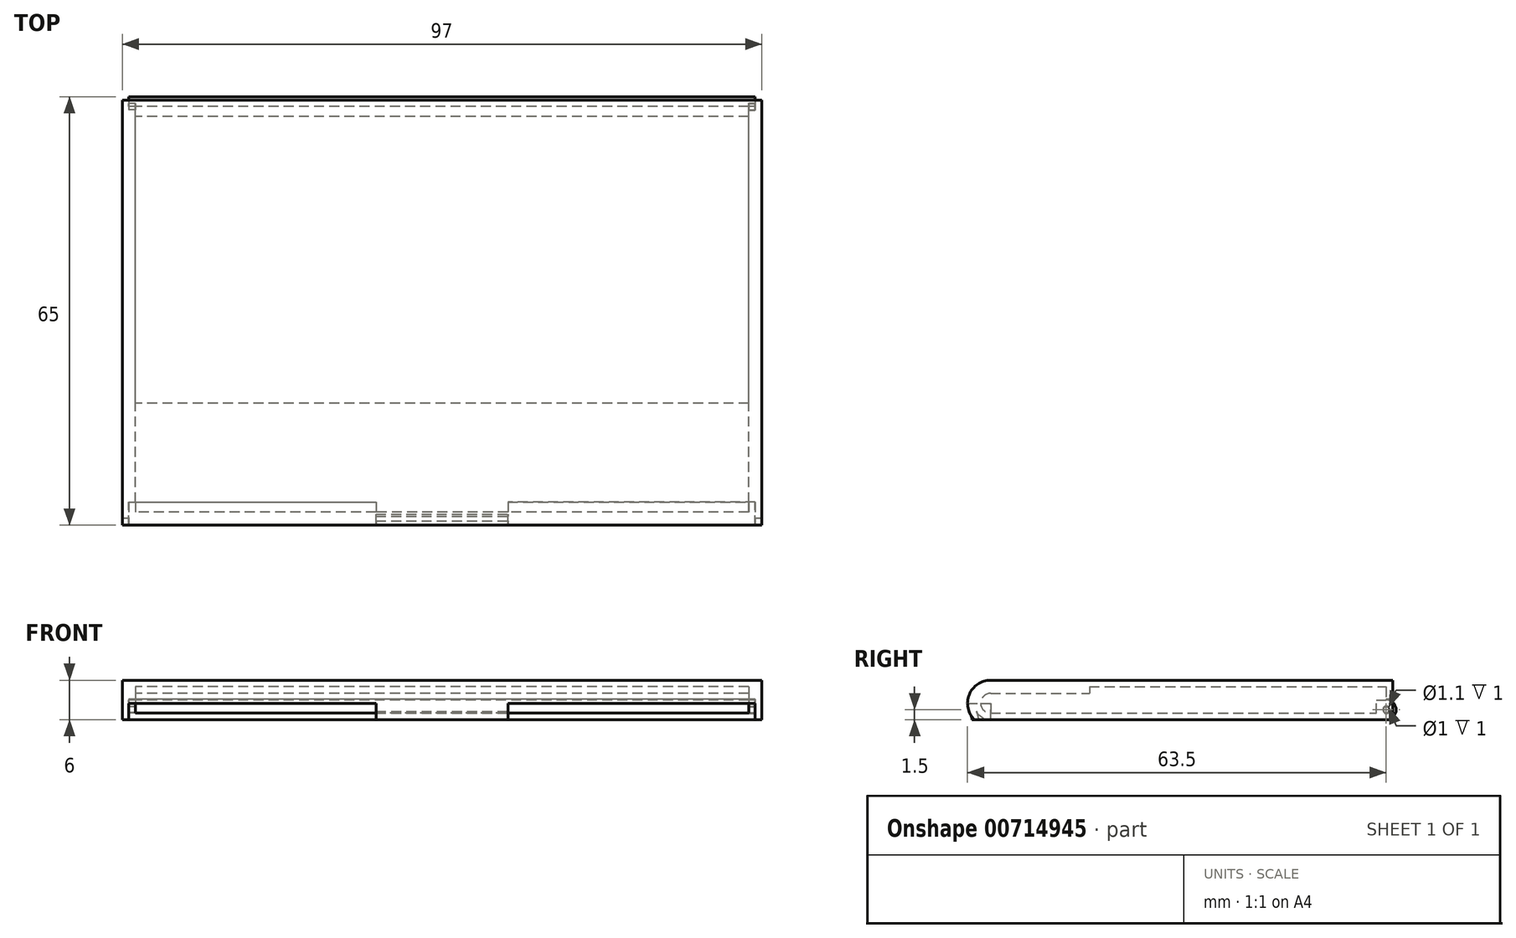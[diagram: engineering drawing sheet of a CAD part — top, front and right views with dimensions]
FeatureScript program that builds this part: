
annotation { "Feature Type Name" : "Feature", "Feature Type Description" : "" }
export const myFeature = defineFeature(function(context is Context, id is Id, definition is map)
    precondition{}
    {
        {
            var Q0;
            Q0=qCreatedBy(makeId("Right.planeOp"),FACE);
            var sketch = newSketch(context, id + "F0", { "sketchPlane" : qUnion([Q0])});
            skLineSegment(sketch, "E0", {"start": v(0, 7.84) * mm, "end": v(0, -7.77) * mm, "construction": true});
            skLineSegment(sketch, "E1", {"start": v(-35.57, 0) * mm, "end": v(44.83, 0) * mm, "construction": true});
            skLineSegment(sketch, "E2.bottom", {"start": v(-30, 2.5) * mm, "end": v(30, 2.5) * mm});
            skLineSegment(sketch, "E2.top", {"start": v(-30, -2.5) * mm, "end": v(30, -2.5) * mm});
            skArc(sketch, "E3", {"start": v(-30, 2.5) * mm, "mid": v(-32.5, 0) * mm, "end": v(-30, -2.5) * mm});
            skPoint(sketch, "E4", {"position": v(0, 2.5) * mm});
            skPoint(sketch, "E5", {"position": v(0, -2.5) * mm});
            skLineSegment(sketch, "E6", {"start": v(30, 2.5) * mm, "end": v(30, -2.5) * mm});
            skSolve(sketch);
        }
        {
            var Q0;
            Q0 = qSketchRegion(id + "F0", true);
            extrude(context, id + "F1", {"entities" : qUnion([Q0]), "endBound" : BoundingType.SYMMETRIC, "depth" : 95 * mm, "offsetDistance" : 25 * mm});
        }
        {
            var Q0;
            Q0=makeQuery(id+"F1.opExtrude","SWEPT_FACE",FACE,{"disambiguationData":[OSD([sQuery(id+"F0.wireOp",EDGE,"E2.bottom")])]});
            var Q1;
            Q1=makeQuery(id+"F1.opExtrude","SWEPT_FACE",FACE,{"disambiguationData":[OSD([sQuery(id+"F0.wireOp",EDGE,"E6")])]});
            shell(context, id + "F2", {"entities" : qUnion([Q0, Q1]), "thickness" : 1 * mm});
        }
        {
            var Q0;
            Q0=qCreatedBy(makeId("Right.planeOp"),FACE);
            var sketch = newSketch(context, id + "F3", { "sketchPlane" : qUnion([Q0])});
            skLineSegment(sketch, "E7.bottom", {"start": v(-30, 2.5) * mm, "end": v(-15, 2.5) * mm});
            skLineSegment(sketch, "E7.top", {"start": v(-30, 1.5) * mm, "end": v(-15, 1.5) * mm});
            skLineSegment(sketch, "E7.left", {"start": v(-30, 2.5) * mm, "end": v(-30, 1.5) * mm});
            skLineSegment(sketch, "E7.right", {"start": v(-15, 2.5) * mm, "end": v(-15, 1.5) * mm});
            skSolve(sketch);
        }
        {
            var Q0;
            Q0 = qSketchRegion(id + "F3", true);
            extrude(context, id + "F4", {"entities" : qUnion([Q0]), "operationType" : NewBodyOperationType.ADD, "endBound" : BoundingType.UP_TO_NEXT, "depth" : 25 * mm, "offsetDistance" : 25 * mm, "hasSecondDirection" : true, "secondDirectionBound" : SecondDirectionBoundingType.UP_TO_NEXT, "secondDirectionOppositeDirection" : true, "secondDirectionDepth" : 25 * mm});
        }
        {
            var Q0;
            Q0=qCreatedBy(makeId("Right.planeOp"),FACE);
            var sketch = newSketch(context, id + "F5", { "sketchPlane" : qUnion([Q0])});
            skArc(sketch, "E8", {"start": v(29.98, -2.5) * mm, "mid": v(31.5, -1) * mm, "end": v(30, 0.5) * mm});
            skLineSegment(sketch, "E9.bottom", {"start": v(30, 0.5) * mm, "end": v(28.5, 0.5) * mm});
            skLineSegment(sketch, "E9.top", {"start": v(30, -2.5) * mm, "end": v(28.5, -2.5) * mm});
            skLineSegment(sketch, "E9.left", {"start": v(30, 0.5) * mm, "end": v(30, -2.5) * mm});
            skLineSegment(sketch, "E9.right", {"start": v(28.5, 0.5) * mm, "end": v(28.5, -2.5) * mm});
            skSolve(sketch);
        }
        {
            var Q0;
            Q0 = qSketchRegion(id + "F5", true);
            var Q1;
            Q1=makeQuery(id+"F1.opExtrude","CAP_FACE",FACE,{"disambiguationData":[OSD([sQuery(id+"F0.wireOp",EDGE,"E2.bottom"),sQuery(id+"F0.wireOp",EDGE,"E2.top"),sQuery(id+"F0.wireOp",EDGE,"E3"),sQuery(id+"F0.wireOp",EDGE,"E6")])],"isStart":false});
            var Q2;
            Q2=makeQuery(id+"F1.opExtrude","CAP_FACE",FACE,{"disambiguationData":[OSD([sQuery(id+"F0.wireOp",EDGE,"E2.bottom"),sQuery(id+"F0.wireOp",EDGE,"E2.top"),sQuery(id+"F0.wireOp",EDGE,"E3"),sQuery(id+"F0.wireOp",EDGE,"E6")])],"isStart":true});
            extrude(context, id + "F6", {"entities" : qUnion([Q0]), "operationType" : NewBodyOperationType.ADD, "endBound" : BoundingType.UP_TO_SURFACE, "depth" : 25 * mm, "endBoundEntityFace" : qUnion([Q1]), "offsetDistance" : 25 * mm, "hasSecondDirection" : true, "secondDirectionBound" : SecondDirectionBoundingType.UP_TO_SURFACE, "secondDirectionOppositeDirection" : true, "secondDirectionDepth" : 25 * mm, "secondDirectionBoundEntityFace" : qUnion([Q2])});
        }
        {
            var Q0;
            Q0=makeQuery(id+"F6.boolean.opBoolean","MERGE",FACE,{"derivedFrom":[makeQuery(id+"F1.opExtrude","CAP_FACE",FACE,{"disambiguationData":[OSD([sQuery(id+"F0.wireOp",EDGE,"E2.bottom"),sQuery(id+"F0.wireOp",EDGE,"E2.top"),sQuery(id+"F0.wireOp",EDGE,"E3"),sQuery(id+"F0.wireOp",EDGE,"E6")])],"isStart":false}),makeQuery(id+"F6.opExtrude","CAP_FACE",FACE,{"disambiguationData":[OSD([sQuery(id+"F5.wireOp",EDGE,"E8"),sQuery(id+"F5.wireOp",EDGE,"E9.bottom"),sQuery(id+"F5.wireOp",EDGE,"E9.top"),sQuery(id+"F5.wireOp",EDGE,"E9.right")])],"isStart":false})]});
            var sketch = newSketch(context, id + "F7", { "sketchPlane" : qUnion([Q0])});
            skCircle(sketch, "E10", {"center": v(30, -1) * mm, "radius": 0.55 * mm});
            skSolve(sketch);
        }
        {
            var Q0;
            Q0 = qSketchRegion(id + "F7", true);
            extrude(context, id + "F8", {"entities" : qUnion([Q0]), "operationType" : NewBodyOperationType.REMOVE, "oppositeDirection" : true, "depth" : 1 * mm, "offsetDistance" : 25 * mm});
        }
        {
            var Q0;
            Q0=makeQuery(id+"F6.boolean.opBoolean","MERGE",FACE,{"derivedFrom":[makeQuery(id+"F1.opExtrude","CAP_FACE",FACE,{"disambiguationData":[OSD([sQuery(id+"F0.wireOp",EDGE,"E2.bottom"),sQuery(id+"F0.wireOp",EDGE,"E2.top"),sQuery(id+"F0.wireOp",EDGE,"E3"),sQuery(id+"F0.wireOp",EDGE,"E6")])],"isStart":true}),makeQuery(id+"F6.opExtrude","CAP_FACE",FACE,{"disambiguationData":[OSD([sQuery(id+"F5.wireOp",EDGE,"E8"),sQuery(id+"F5.wireOp",EDGE,"E9.bottom"),sQuery(id+"F5.wireOp",EDGE,"E9.top"),sQuery(id+"F5.wireOp",EDGE,"E9.right")])],"isStart":true})]});
            var sketch = newSketch(context, id + "F9", { "sketchPlane" : qUnion([Q0])});
            skCircle(sketch, "E11", {"center": v(-30, -1) * mm, "radius": 0.5 * mm});
            skSolve(sketch);
        }
        {
            var Q0;
            Q0 = qSketchRegion(id + "F9", true);
            extrude(context, id + "F10", {"entities" : qUnion([Q0]), "operationType" : NewBodyOperationType.REMOVE, "oppositeDirection" : true, "depth" : 1 * mm, "offsetDistance" : 25 * mm});
        }
        {
            var Q0;
            Q0=qCreatedBy(makeId("Right.planeOp"),FACE);
            var sketch = newSketch(context, id + "F11", { "sketchPlane" : qUnion([Q0])});
            skArc(sketch, "E12", {"start": v(-30, 3.5) * mm, "mid": v(-33.24, 1.32) * mm, "end": v(-32.45, -2.5) * mm});
            skLineSegment(sketch, "E13.bottom", {"start": v(-30, 3.5) * mm, "end": v(31, 3.5) * mm});
            skLineSegment(sketch, "E13.top", {"start": v(-30, -2.5) * mm, "end": v(31, -2.5) * mm});
            skLineSegment(sketch, "E13.right", {"start": v(31, 3.5) * mm, "end": v(31, -2.5) * mm});
            skLineSegment(sketch, "E14", {"start": v(-30, -2.5) * mm, "end": v(-32.45, -2.5) * mm});
            skSolve(sketch);
        }
        {
            var Q0;
            Q0 = qSketchRegion(id + "F11", true);
            extrude(context, id + "F12", {"entities" : qUnion([Q0]), "endBound" : BoundingType.SYMMETRIC, "depth" : (95 + 2) * mm, "offsetDistance" : 25 * mm});
        }
        {
            var Q0;
            Q0=makeQuery(id+"F12.opExtrude","SWEPT_FACE",FACE,{"disambiguationData":[OSD([sQuery(id+"F11.wireOp",EDGE,"E13.top"),sQuery(id+"F11.wireOp",EDGE,"E14")])]});
            var Q1;
            Q1=makeQuery(id+"F12.opExtrude","SWEPT_FACE",FACE,{"disambiguationData":[OSD([sQuery(id+"F11.wireOp",EDGE,"E13.right")])]});
            shell(context, id + "F13", {"entities" : qUnion([Q0, Q1]), "thickness" : 1 * mm});
        }
        {
            var Q0;
            Q0=qCreatedBy(makeId("Front.planeOp"),FACE);
            cPlane(context, id + "F14", {"entities" : qUnion([Q0]), "cplaneType" : CPlaneType.OFFSET, "offset" : 30 * mm, "width" : 150 * mm, "height" : 150 * mm});
        }
        {
            var Q0;
            Q0=qCreatedBy(id+"F14.planeOp",FACE);
            var sketch = newSketch(context, id + "F15", { "sketchPlane" : qUnion([Q0])});
            skLineSegment(sketch, "E15.bottom", {"start": v(-47.5, -10.67) * mm, "end": v(-10, -10.67) * mm});
            skLineSegment(sketch, "E15.top", {"start": v(-47.5, 0) * mm, "end": v(-10, 0) * mm});
            skLineSegment(sketch, "E15.left", {"start": v(-47.5, -10.67) * mm, "end": v(-47.5, 0) * mm});
            skLineSegment(sketch, "E15.right", {"start": v(-10, -10.67) * mm, "end": v(-10, 0) * mm});
            skLineSegment(sketch, "E16", {"start": v(0, 0) * mm, "end": v(0, 8.87) * mm, "construction": true});
            skLineSegment(sketch, "E17", {"start": v(0, 0) * mm, "end": v(-7.82, 0) * mm, "construction": true});
            skLineSegment(sketch, "E18.MirrorCS", {"start": v(10, -10.67) * mm, "end": v(10, 0) * mm});
            skLineSegment(sketch, "E19.MirrorCS", {"start": v(47.5, -10.67) * mm, "end": v(10, -10.67) * mm});
            skLineSegment(sketch, "E20.MirrorCS", {"start": v(47.5, -10.67) * mm, "end": v(47.5, 0) * mm});
            skLineSegment(sketch, "E21.MirrorCS", {"start": v(47.5, 0) * mm, "end": v(10, 0) * mm});
            skSolve(sketch);
        }
        {
            var Q0;
            Q0 = qSketchRegion(id + "F15", true);
            var Q1;
            Q1=makeQuery(id+"F12.opExtrude","SWEPT_FACE",FACE,{"disambiguationData":[OSD([sQuery(id+"F11.wireOp",EDGE,"E12")])]});
            extrude(context, id + "F16", {"entities" : qUnion([Q0]), "operationType" : NewBodyOperationType.REMOVE, "endBound" : BoundingType.UP_TO_SURFACE, "depth" : 25 * mm, "endBoundEntityFace" : qUnion([Q1]), "offsetDistance" : 25 * mm});
        }
        {
            var Q0;
            Q0=makeQuery(id+"F16.boolean.opBoolean","COPY",FACE,{"derivedFrom":makeQuery(id+"F16.opExtrude","SWEPT_FACE",FACE,{"disambiguationData":[OSD([sQuery(id+"F15.wireOp",EDGE,"E18.MirrorCS")])]})});
            var sketch = newSketch(context, id + "F17", { "sketchPlane" : qUnion([Q0])});
            skPoint(sketch, "E22.orphan", {"position": v(-32.5, 0) * mm});
            skPoint(sketch, "E23.0.start.orphan", {"position": v(-33.5, 0) * mm});
            skLineSegment(sketch, "E24", {"start": v(-33.03, -1.75) * mm, "end": v(-32.17, -1.25) * mm});
            skArc(sketch, "E25.0", {"start": v(-30, -2.5) * mm, "mid": v(-31.25, -2.17) * mm, "end": v(-32.17, -1.25) * mm});
            skLineSegment(sketch, "E26.0", {"start": v(-32.45, -2.5) * mm, "end": v(-30, -2.5) * mm});
            skArc(sketch, "E27.0", {"start": v(-33.03, -1.75) * mm, "mid": v(-32.77, -2.14) * mm, "end": v(-32.45, -2.5) * mm});
            skSolve(sketch);
        }
        {
            var Q0;
            Q0 = qSketchRegion(id + "F17", true);
            var Q1;
            Q1=makeQuery(id+"F16.boolean.opBoolean","COPY",FACE,{"derivedFrom":makeQuery(id+"F16.opExtrude","SWEPT_FACE",FACE,{"disambiguationData":[OSD([sQuery(id+"F15.wireOp",EDGE,"E15.right")])]})});
            extrude(context, id + "F18", {"entities" : qUnion([Q0]), "operationType" : NewBodyOperationType.REMOVE, "endBound" : BoundingType.UP_TO_SURFACE, "oppositeDirection" : true, "depth" : 25 * mm, "endBoundEntityFace" : qUnion([Q1]), "offsetDistance" : 25 * mm});
        }
        {
            var Q0;
            Q0=makeQuery(id+"F16.boolean.opBoolean","COPY",FACE,{"derivedFrom":makeQuery(id+"F16.opExtrude","SWEPT_FACE",FACE,{"disambiguationData":[OSD([sQuery(id+"F15.wireOp",EDGE,"E18.MirrorCS")])]})});
            var sketch = newSketch(context, id + "F19", { "sketchPlane" : qUnion([Q0])});
            skArc(sketch, "E28", {"start": v(-32.83, -2.5) * mm, "mid": v(-32.88, -2.11) * mm, "end": v(-33.03, -1.75) * mm});
            skArc(sketch, "E29", {"start": v(-31.83, -2.5) * mm, "mid": v(-31.92, -1.85) * mm, "end": v(-32.17, -1.25) * mm});
            skPoint(sketch, "E30.0", {"position": v(-32.41, -0.65) * mm});
            skLineSegment(sketch, "E31", {"start": v(-29.9, 0.06) * mm, "end": v(-34.33, -2.5) * mm, "construction": true});
            skLineSegment(sketch, "E32", {"start": v(-32.83, -2.5) * mm, "end": v(-31.83, -2.5) * mm});
            skLineSegment(sketch, "E33", {"start": v(-33.03, -1.75) * mm, "end": v(-32.17, -1.25) * mm});
            skPoint(sketch, "E34.0.start.orphan", {"position": v(-33.5, 0) * mm});
            skPoint(sketch, "E35.0.end.orphan", {"position": v(-32.5, 0) * mm});
            skSolve(sketch);
        }
        {
            var Q0;
            Q0 = qSketchRegion(id + "F19", true);
            var Q1;
            Q1=makeQuery(id+"F16.boolean.opBoolean","COPY",FACE,{"derivedFrom":makeQuery(id+"F16.opExtrude","SWEPT_FACE",FACE,{"disambiguationData":[OSD([sQuery(id+"F15.wireOp",EDGE,"E15.right")])]})});
            extrude(context, id + "F20", {"entities" : qUnion([Q0]), "operationType" : NewBodyOperationType.ADD, "endBound" : BoundingType.UP_TO_SURFACE, "oppositeDirection" : true, "depth" : 25 * mm, "endBoundEntityFace" : qUnion([Q1]), "offsetDistance" : 25 * mm});
        }
        {
            var Q0;
            Q0=qCreatedBy(makeId("Right.planeOp"),FACE);
            var sketch = newSketch(context, id + "F21", { "sketchPlane" : qUnion([Q0])});
            skLineSegment(sketch, "E36.bottom", {"start": v(30, 3.5) * mm, "end": v(31, 3.5) * mm});
            skLineSegment(sketch, "E36.top", {"start": v(30, 0.6) * mm, "end": v(31, 0.6) * mm});
            skLineSegment(sketch, "E36.left", {"start": v(30, 3.5) * mm, "end": v(30, 0.6) * mm});
            skLineSegment(sketch, "E36.right", {"start": v(31, 3.5) * mm, "end": v(31, 0.6) * mm});
            skSolve(sketch);
        }
        {
            var Q0;
            Q0 = qSketchRegion(id + "F21", true);
            var Q1;
            Q1=makeQuery(id+"F12.opExtrude","CAP_FACE",FACE,{"disambiguationData":[OSD([sQuery(id+"F11.wireOp",EDGE,"E12"),sQuery(id+"F11.wireOp",EDGE,"E13.bottom"),sQuery(id+"F11.wireOp",EDGE,"E13.top"),sQuery(id+"F11.wireOp",EDGE,"E13.right"),sQuery(id+"F11.wireOp",EDGE,"E14")])],"isStart":false});
            var Q2;
            Q2=makeQuery(id+"F12.opExtrude","CAP_FACE",FACE,{"disambiguationData":[OSD([sQuery(id+"F11.wireOp",EDGE,"E12"),sQuery(id+"F11.wireOp",EDGE,"E13.bottom"),sQuery(id+"F11.wireOp",EDGE,"E13.top"),sQuery(id+"F11.wireOp",EDGE,"E13.right"),sQuery(id+"F11.wireOp",EDGE,"E14")])],"isStart":true});
            extrude(context, id + "F22", {"entities" : qUnion([Q0]), "operationType" : NewBodyOperationType.ADD, "endBound" : BoundingType.UP_TO_SURFACE, "depth" : 25 * mm, "endBoundEntityFace" : qUnion([Q1]), "offsetDistance" : 25 * mm, "hasSecondDirection" : true, "secondDirectionBound" : SecondDirectionBoundingType.UP_TO_SURFACE, "secondDirectionOppositeDirection" : true, "secondDirectionDepth" : 25 * mm, "secondDirectionBoundEntityFace" : qUnion([Q2])});
        }
        {
            var Q0;
            {var subQ0=sQuery(id+"F11.wireOp",EDGE,"E14");var subQ1=sQuery(id+"F11.wireOp",EDGE,"E13.right");var subQ2=sQuery(id+"F11.wireOp",EDGE,"E13.top");var subQ3=sQuery(id+"F11.wireOp",EDGE,"E13.bottom");var subQ4=sQuery(id+"F11.wireOp",EDGE,"E12");Q0=makeQuery(id+"F16.boolean.opBoolean","MERGE",FACE,{"derivedFrom":[makeQuery(id+"F13.opShell","OFFSET_FACE",FACE,{"disambiguationData":[OSD([subQ4,subQ3,subQ2,subQ1,subQ0]),TDD([makeQuery(id+"F12.opExtrude","CAP_FACE",FACE,{"disambiguationData":[OSD([subQ4,subQ3,subQ2,subQ1,subQ0])],"isStart":true})])]})],"fromTools":[makeQuery(id+"F16.opExtrude","SWEPT_FACE",FACE,{"disambiguationData":[OSD([sQuery(id+"F15.wireOp",EDGE,"E15.left")])]})]});}
            var sketch = newSketch(context, id + "F23", { "sketchPlane" : qUnion([Q0])});
            skCircle(sketch, "E37", {"center": v(30, -1) * mm, "radius": 0.45 * mm});
            skSolve(sketch);
        }
        {
            var Q0;
            Q0 = qSketchRegion(id + "F23", true);
            extrude(context, id + "F24", {"entities" : qUnion([Q0]), "operationType" : NewBodyOperationType.ADD, "depth" : 1.2 * mm, "offsetDistance" : 25 * mm});
        }
        {
            var Q0;
            {var subQ0=sQuery(id+"F11.wireOp",EDGE,"E14");var subQ1=sQuery(id+"F11.wireOp",EDGE,"E13.right");var subQ2=sQuery(id+"F11.wireOp",EDGE,"E13.top");var subQ3=sQuery(id+"F11.wireOp",EDGE,"E13.bottom");var subQ4=sQuery(id+"F11.wireOp",EDGE,"E12");Q0=makeQuery(id+"F16.boolean.opBoolean","MERGE",FACE,{"derivedFrom":[makeQuery(id+"F13.opShell","OFFSET_FACE",FACE,{"disambiguationData":[OSD([subQ4,subQ3,subQ2,subQ1,subQ0]),TDD([makeQuery(id+"F12.opExtrude","CAP_FACE",FACE,{"disambiguationData":[OSD([subQ4,subQ3,subQ2,subQ1,subQ0])],"isStart":false})])]})],"fromTools":[makeQuery(id+"F16.opExtrude","SWEPT_FACE",FACE,{"disambiguationData":[OSD([sQuery(id+"F15.wireOp",EDGE,"E20.MirrorCS")])]})]});}
            var sketch = newSketch(context, id + "F25", { "sketchPlane" : qUnion([Q0])});
            skCircle(sketch, "E38.0", {"center": v(-30, -1) * mm, "radius": 0.45 * mm});
            skSolve(sketch);
        }
        {
            var Q0;
            Q0 = qSketchRegion(id + "F25", true);
            extrude(context, id + "F26", {"entities" : qUnion([Q0]), "operationType" : NewBodyOperationType.ADD, "depth" : 1.2 * mm, "offsetDistance" : 25 * mm});
        }
    });
